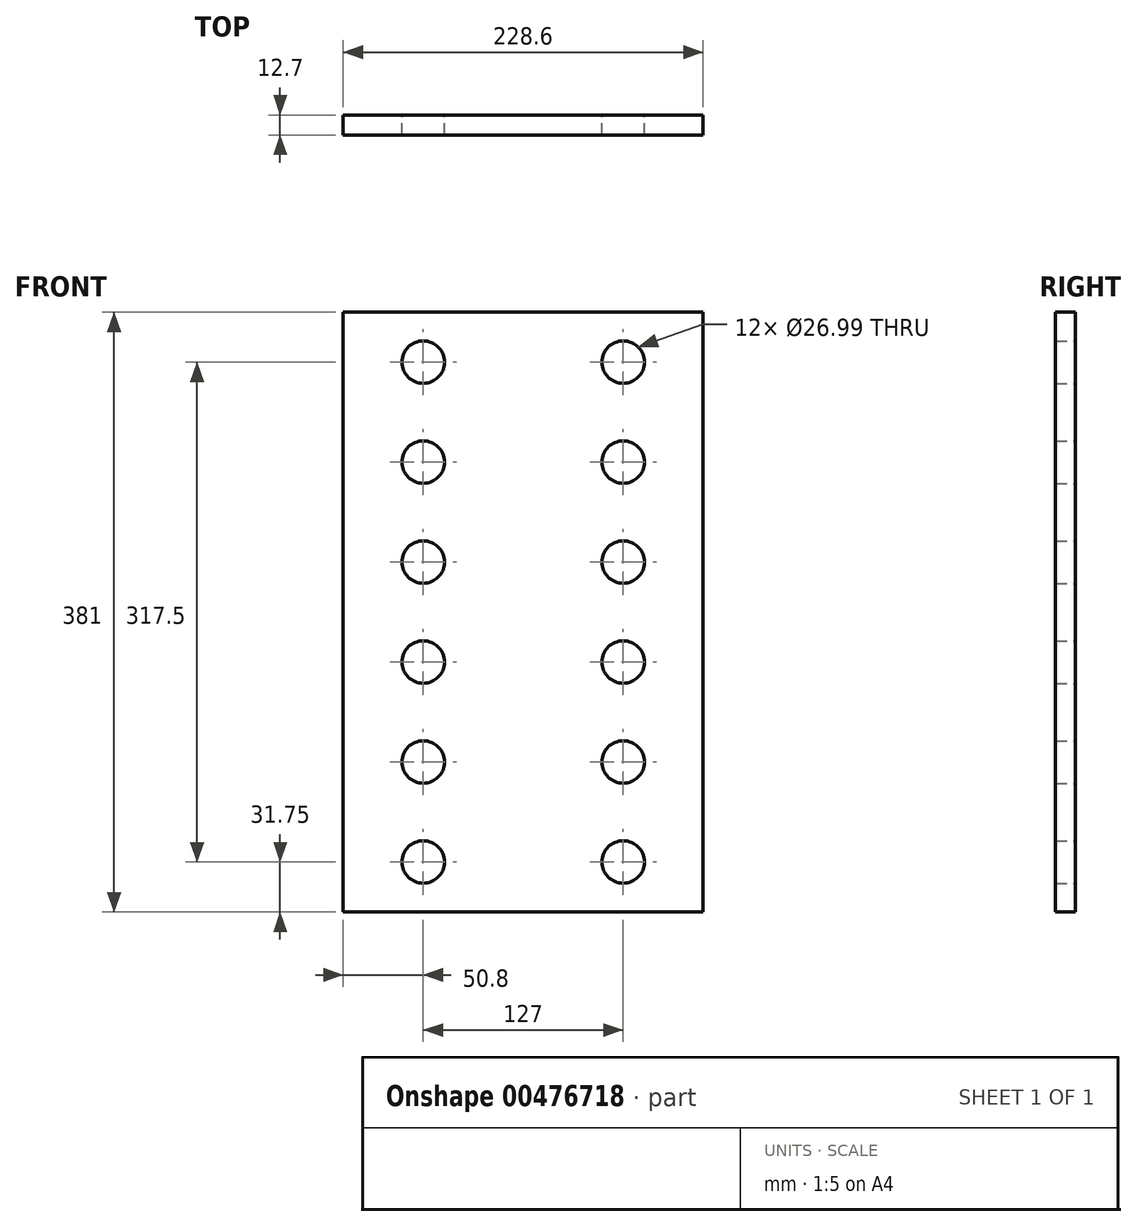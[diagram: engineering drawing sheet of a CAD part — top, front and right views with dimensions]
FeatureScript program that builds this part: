
annotation { "Feature Type Name" : "Feature", "Feature Type Description" : "" }
export const myFeature = defineFeature(function(context is Context, id is Id, definition is map)
    precondition{}
    {
        {
            var Q0;
            Q0=qCreatedBy(makeId("Front.planeOp"),FACE);
            var sketch = newSketch(context, id + "F0", { "sketchPlane" : qUnion([Q0])});
            skLineSegment(sketch, "E0", {"start": v(0, 0) * mm, "end": v(0, 381) * mm});
            skLineSegment(sketch, "E1", {"start": v(0, 381) * mm, "end": v(228.6, 381) * mm});
            skLineSegment(sketch, "E2", {"start": v(228.6, 381) * mm, "end": v(228.6, 0) * mm});
            skLineSegment(sketch, "E3", {"start": v(228.6, 0) * mm, "end": v(0, 0) * mm});
            skPoint(sketch, "E4", {"position": v(177.8, 349.25) * mm});
            skLineSegment(sketch, "E5", {"start": v(114.3, 381) * mm, "end": v(114.3, 0) * mm, "construction": true});
            skPoint(sketch, "E6.0.1.0", {"position": v(177.8, 285.75) * mm});
            skPoint(sketch, "E6.0.2.0", {"position": v(177.8, 222.25) * mm});
            skPoint(sketch, "E6.0.3.0", {"position": v(177.8, 158.75) * mm});
            skPoint(sketch, "E6.0.4.0", {"position": v(177.8, 95.25) * mm});
            skPoint(sketch, "E6.0.5.0", {"position": v(177.8, 31.75) * mm});
            skLineSegment(sketch, "E6.direction1", {"start": v(177.8, 349.25) * mm, "end": v(149.91, 349.25) * mm, "construction": true});
            skLineSegment(sketch, "E6.direction2", {"start": v(177.8, 349.25) * mm, "end": v(177.8, 285.75) * mm, "construction": true});
            skPoint(sketch, "E7.MirrorP", {"position": v(50.8, 95.25) * mm});
            skPoint(sketch, "E8.MirrorP", {"position": v(50.8, 158.75) * mm});
            skPoint(sketch, "E9.MirrorP", {"position": v(50.8, 31.75) * mm});
            skLineSegment(sketch, "E10.MirrorCS", {"start": v(50.8, 349.25) * mm, "end": v(50.8, 285.75) * mm, "construction": true});
            skPoint(sketch, "E11.MirrorP", {"position": v(50.8, 349.25) * mm});
            skPoint(sketch, "E12.MirrorP", {"position": v(50.8, 222.25) * mm});
            skPoint(sketch, "E13.MirrorP", {"position": v(50.8, 285.75) * mm});
            skSolve(sketch);
        }
        {
            var Q0;
            Q0=makeQuery(id+"F0.imprint","IMPRINT",FACE,{"disambiguationData":[TD([[makeQuery(id+"F0.imprint","IMPRINT",EDGE,{"derivedFrom":sQuery(id+"F0.wireOp",EDGE,"E0")}),-1.0]])]});
            extrude(context, id + "F1", {"entities" : qUnion([Q0]), "depth" : 12.7 * mm});
        }
        {
            var Q0;
            Q0=sQuery(id+"F0.wireOp",VERTEX,"E4");
            var Q1;
            Q1=sQuery(id+"F0.wireOp",VERTEX,"E6.direction2.end");
            var Q2;
            Q2=sQuery(id+"F0.wireOp",VERTEX,"E6.0.2.0");
            var Q3;
            Q3=sQuery(id+"F0.wireOp",VERTEX,"E6.0.3.0");
            var Q4;
            Q4=sQuery(id+"F0.wireOp",VERTEX,"E6.0.4.0");
            var Q5;
            Q5=sQuery(id+"F0.wireOp",VERTEX,"E6.0.5.0");
            var Q6;
            Q6=sQuery(id+"F0.wireOp",VERTEX,"E9.MirrorP");
            var Q7;
            Q7=sQuery(id+"F0.wireOp",VERTEX,"E7.MirrorP");
            var Q8;
            Q8=sQuery(id+"F0.wireOp",VERTEX,"E12.MirrorP");
            var Q9;
            Q9=sQuery(id+"F0.wireOp",VERTEX,"E13.MirrorP");
            var Q10;
            Q10=sQuery(id+"F0.wireOp",VERTEX,"E11.MirrorP");
            var Q11;
            Q11=sQuery(id+"F0.wireOp",VERTEX,"E8.MirrorP");
            var Q12;
            Q12=makeQuery(id+"F1.opExtrude","SWEPT_BODY",BODY,{"disambiguationData":[OSD([sQuery(id+"F0.wireOp",EDGE,"E0"),sQuery(id+"F0.wireOp",EDGE,"E1"),sQuery(id+"F0.wireOp",EDGE,"E2"),sQuery(id+"F0.wireOp",EDGE,"E3")])]});
            hole(context, id + "F2", {"style" : HoleStyle.SIMPLE, "endStyle" : HoleEndStyle.BLIND, "oppositeDirection" : true, "holeDiameter" : 26.99 * mm, "holeDepth" : 25.4 * mm, "isTappedThrough" : true, "tappedDepth" : 12.7 * mm, "tapClearance" : 3, "locations" : qUnion([Q0, Q1, Q2, Q3, Q4, Q5, Q6, Q7, Q8, Q9, Q10, Q11]), "scope" : qUnion([Q12])});
        }
    });
